# Revit family: Ginko 2.4
name_source: partatom
category: Lighting Fixtures
revit_build: Autodesk Revit 2017 (Build: 20160225_1515(x64)
units: mm (PartAtom-declared; Revit-internal decimal feet)

## family parameters
Always vertical = No
Cut with Voids When Loaded = No
Light Source = No
OmniClass Number = 23.80.70.00
OmniClass Title = Lighting
Part Type = Normal
Room Calculation Point = Yes
Round Connector Dimension = Use Diameter
Shared = No
Work Plane-Based = Yes

## types (4) — shared parameters
Apparent Load Phase 1 = 7 W
Base = L&L_White
Base bracket = Ginko2.0_Base bracket
Bracket = L&L_Stainless steel
CRI = 90 (also available: CRI 80 - ref. URL Technical sheet)
Code = GN2401 R1 E White; GN2401 R1 N Black anodized; GN2401 R1 F Grey; GN2401 R1 H Anthracite; GN2232 R1 T Cor-ten; GN2401 R1 5 Jasper green
Control system = -
Cutout dimensions = -
Default Elevation = 1219 mm
Delivered lumen output = 122 lm (3000K, 36°, CRI 80); 113 lm (3000K, 36°, CRI 90)
Description = Outdoor projectors
Energy efficiency class = A A+ A++
Features = -
Geometry = Ginko2.4_mod : Ginko_2.4
H1 = 55 mm  [stored 0.180446 ft]
Height mm = 125 mm  [stored 0.410105 ft]
IP = 66
LED Colour = 3000K (also available: 2700K and 4000K - ref. URL Technical sheet)
Length mm = 83 mm  [stored 0.27231 ft]
Lens = L&L_Lens
Lumen output at source = 657 lm (3000K, CRI 80), 608 lm (3000K, CRI 90)
Manufacturer = L&L Luce&Light
Material = body in anticorodal aluminium, AISI 316L stainless steel bracket, screen in tempered, transparent extra-clear glass
Middle = L&L_White
Model = Ginko 2.4
Mounting = surface mounted (ceiling, wall, ground, spike)
No. and type of led = 1 high intensity power LED; 3-step MacAdam; 50000h L90 B10 (Ta 25°C)
Notes = -
Power = 7W
Power cables = includes 1,5 m neoprene cable, H05RN-F 2x0,75/0,75 Ø6,3 mm
Power supply = 24Vdc
Power supply unit = not included
Top = L&L_White
URL = https://www.lucelight.it
URL Accessories and power supply units = https://www.lucelight.it
URL Catalogue = https://www.lucelight.it
URL DXF = https://www.lucelight.it
URL Description = https://www.lucelight.it
URL General code = https://www.lucelight.it
URL IES Photometric file = https://www.lucelight.it
URL Image = https://www.lucelight.it
URL Technical sheet = https://www.lucelight.it
Vertical rotation max = 190.00°
Voltage = 24 V
Weight kg = 0.45
Width mm = 54 mm  [stored 0.177165 ft]
Wiring = -
X1 = 100 mm  [stored 0.328084 ft]

## per-type parameters (varying)
| type | Light Source | Optics |
| Ginko 2.4_ R1_zoom 18° (3000K 7W 24 Vdc) | Light Source_2.4 : R1_zoom 18° | 18° |
| Ginko 2.4_ R1_zoom 31° (3000K 7W 24 Vdc) | Light Source_2.4 : R1_zoom 31° | 31° |
| Ginko 2.4_ R1_zoom 36° (3000K 7W 24 Vdc) | Light Source_2.4 : R1_zoom 36° | 36° |
| Ginko 2.4_ R1_zoom 9° (3000K 7W 24 Vdc) | Light Source_2.4 : R1_zoom 9° | 9° |

note: [stored X ft] marks values corroborated as IEEE doubles in the binary element streams (Revit-internal decimal feet)

## geometry (parser evidence)
native form markers: Blend x2, Sweep x7
no freeform markers — native parametric forms only
